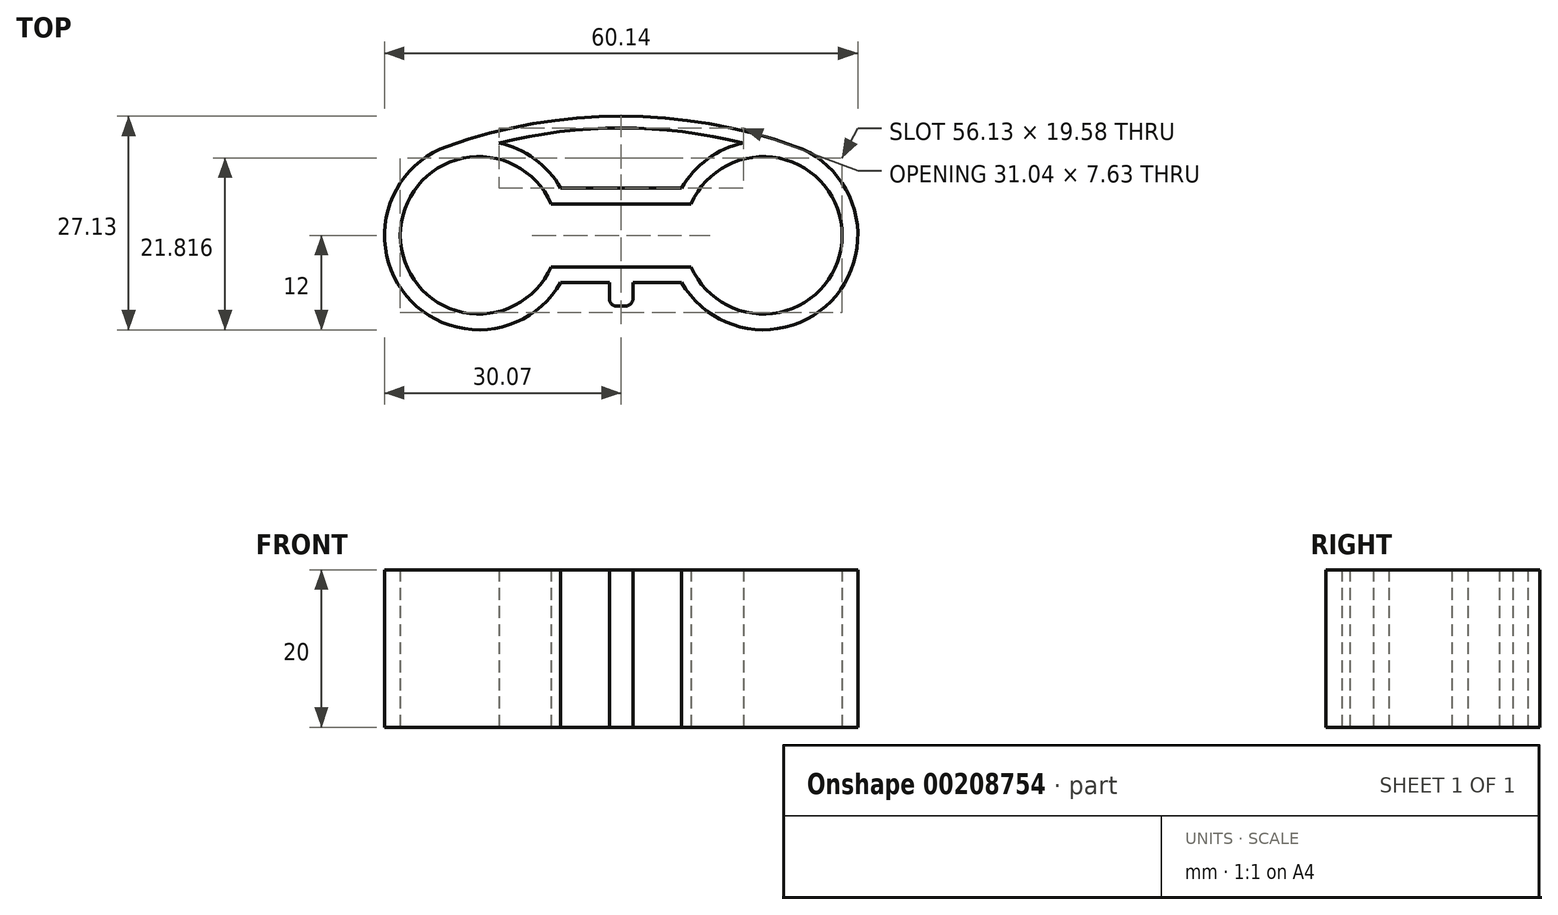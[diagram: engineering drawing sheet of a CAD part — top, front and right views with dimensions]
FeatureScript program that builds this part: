
annotation { "Feature Type Name" : "Feature", "Feature Type Description" : "" }
export const myFeature = defineFeature(function(context is Context, id is Id, definition is map)
    precondition{}
    {
        {
            var Q0;
            Q0=qCreatedBy(makeId("Top.planeOp"),FACE);
            var sketch = newSketch(context, id + "F0", { "sketchPlane" : qUnion([Q0])});
            skLineSegment(sketch, "E0", {"start": v(0, 4) * mm, "end": v(-8.9, 4) * mm});
            skArc(sketch, "E1", {"start": v(-8.9, 4) * mm, "mid": v(-28.07, 0) * mm, "end": v(-8.9, -4) * mm});
            skLineSegment(sketch, "E2", {"start": v(0, 4) * mm, "end": v(8.9, 4) * mm});
            skArc(sketch, "E3", {"start": v(8.9, -4) * mm, "mid": v(28.07, 0) * mm, "end": v(8.9, 4) * mm});
            skLineSegment(sketch, "E4", {"start": v(-8.9, -4) * mm, "end": v(8.9, -4) * mm});
            skPoint(sketch, "E5.start.orphan", {"position": v(-7.6, 0) * mm});
            skPoint(sketch, "E6.start.orphan", {"position": v(7.6, 0) * mm});
            skLineSegment(sketch, "E7.0", {"start": v(-7.67, -6) * mm, "end": v(7.67, -6) * mm});
            skArc(sketch, "E7.1", {"start": v(-7.67, 6) * mm, "mid": v(-30.07, 0) * mm, "end": v(-7.67, -6) * mm});
            skArc(sketch, "E7.2", {"start": v(7.67, -6) * mm, "mid": v(30.07, 0) * mm, "end": v(7.67, 6) * mm});
            skLineSegment(sketch, "E7.3", {"start": v(-1.3, 6) * mm, "end": v(7.67, 6) * mm});
            skLineSegment(sketch, "E7.4", {"start": v(-1.3, 6) * mm, "end": v(-7.67, 6) * mm});
            skPoint(sketch, "E8.end.orphan", {"position": v(0, -4) * mm});
            skArc(sketch, "E9", {"start": v(22.1, 11.3) * mm, "mid": v(0, 15.13) * mm, "end": v(-22.1, 11.3) * mm});
            skArc(sketch, "E10.0", {"start": v(15.52, 11.73) * mm, "mid": v(0, 13.63) * mm, "end": v(-15.52, 11.73) * mm});
            skSolve(sketch);
        }
        {
            var Q0;
            Q0=makeQuery(id+"F0.imprint","IMPRINT",FACE,{"disambiguationData":[TD([[makeQuery(id+"F0.imprint","IMPRINT",EDGE,{"derivedFrom":sQuery(id+"F0.wireOp",EDGE,"E0")}),-1.0]])]});
            var Q1;
            {var subQ0=sQuery(id+"F0.wireOp",EDGE,"E9");Q1=makeQuery(id+"F0.imprint","IMPRINT",FACE,{"disambiguationData":[TD([[makeQuery(id+"F0.imprint","IMPRINT",EDGE,{"derivedFrom":subQ0}),1.0]])]});}
            extrude(context, id + "F1", {"entities" : qUnion([Q0, Q1]), "depth" : 20 * mm});
        }
        {
            var Q0;
            Q0=makeQuery(id+"F1.opExtrude","SWEPT_FACE",FACE,{"disambiguationData":[OSD([sQuery(id+"F0.wireOp",EDGE,"E7.0")])]});
            var sketch = newSketch(context, id + "F2", { "sketchPlane" : qUnion([Q0])});
            skLineSegment(sketch, "E11", {"start": v(0, 20) * mm, "end": v(-1.5, 20) * mm});
            skLineSegment(sketch, "E12", {"start": v(-1.5, 20) * mm, "end": v(-1.5, 0) * mm});
            skLineSegment(sketch, "E13", {"start": v(-1.5, 0) * mm, "end": v(0, 0) * mm});
            skLineSegment(sketch, "E14", {"start": v(1.5, 20) * mm, "end": v(1.5, 0) * mm});
            skLineSegment(sketch, "E15", {"start": v(1.5, 0) * mm, "end": v(0, 0) * mm});
            skSolve(sketch);
        }
        {
            var Q0;
            {var subQ1=sQuery(id+"F2.wireOp",EDGE,"E11");Q0=makeQuery(id+"F2.imprint","IMPRINT",FACE,{"disambiguationData":[TD([[makeQuery(id+"F2.imprint","IMPRINT",EDGE,{"derivedFrom":subQ1}),-1.0]])]});}
            extrude(context, id + "F3", {"entities" : qUnion([Q0]), "operationType" : NewBodyOperationType.ADD, "depth" : 3 * mm});
        }
        {
            var Q0;
            Q0=makeQuery(id+"F3.opExtrude","CAP_EDGE",EDGE,{"disambiguationData":[OSD([sQuery(id+"F2.wireOp",EDGE,"E14")])],"isStart":false});
            var Q1;
            Q1=makeQuery(id+"F3.opExtrude","CAP_EDGE",EDGE,{"disambiguationData":[OSD([sQuery(id+"F2.wireOp",EDGE,"E12")])],"isStart":false});
            fillet(context, id + "F4", {"entities" : qUnion([Q0, Q1]), "radius" : 1 * mm, "tangentPropagation" : true, "allowEdgeOverflow" : false});
        }
    });
